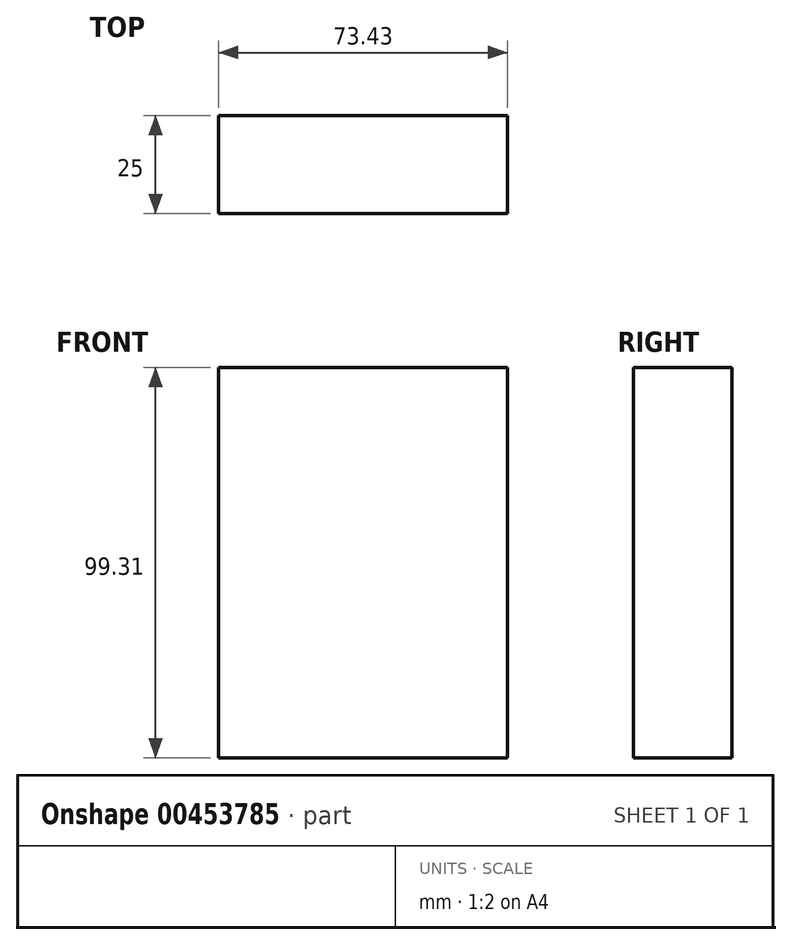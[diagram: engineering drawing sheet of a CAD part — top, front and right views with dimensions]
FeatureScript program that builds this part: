
annotation { "Feature Type Name" : "Feature", "Feature Type Description" : "" }
export const myFeature = defineFeature(function(context is Context, id is Id, definition is map)
    precondition{}
    {
        {
            var Q0;
            Q0=qCreatedBy(makeId("Front.planeOp"),FACE);
            var sketch = newSketch(context, id + "F0", { "sketchPlane" : qUnion([Q0])});
            skLineSegment(sketch, "E0.bottom", {"start": v(-132.18, -8.12) * mm, "end": v(-58.75, -8.12) * mm});
            skLineSegment(sketch, "E0.top", {"start": v(-132.18, 91.19) * mm, "end": v(-58.75, 91.19) * mm});
            skLineSegment(sketch, "E0.left", {"start": v(-132.18, -8.12) * mm, "end": v(-132.18, 91.19) * mm});
            skLineSegment(sketch, "E0.right", {"start": v(-58.75, -8.12) * mm, "end": v(-58.75, 91.19) * mm});
            skPoint(sketch, "E0.middle", {"position": v(-95.46, 41.54) * mm});
            skSolve(sketch);
        }
        {
            var Q0;
            Q0=makeQuery(id+"F0.imprint","IMPRINT",FACE,{"disambiguationData":[TD([[makeQuery(id+"F0.imprint","IMPRINT",EDGE,{"derivedFrom":sQuery(id+"F0.wireOp",EDGE,"E0.bottom")}),1.0]])]});
            extrude(context, id + "F1", {"entities" : qUnion([Q0]), "depth" : 25 * mm});
        }
    });
